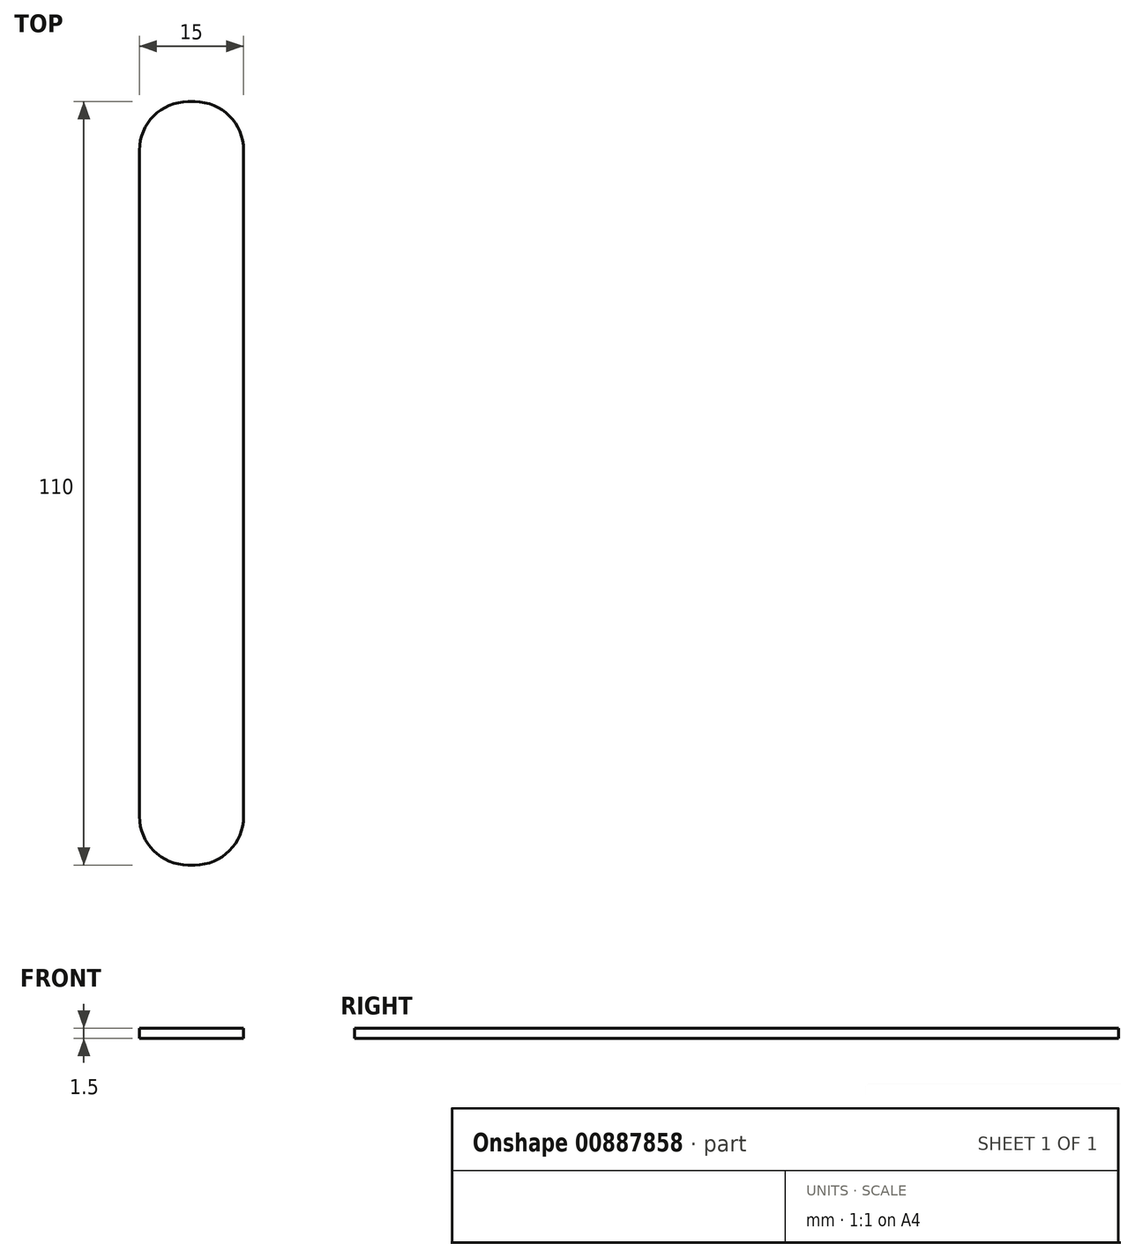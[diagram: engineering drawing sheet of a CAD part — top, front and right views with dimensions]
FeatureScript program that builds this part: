
annotation { "Feature Type Name" : "Feature", "Feature Type Description" : "" }
export const myFeature = defineFeature(function(context is Context, id is Id, definition is map)
    precondition{}
    {
        {
            var Q0;
            Q0=qCreatedBy(makeId("Top.planeOp"),FACE);
            var sketch = newSketch(context, id + "F0", { "sketchPlane" : qUnion([Q0])});
            skLineSegment(sketch, "E0.bottom", {"start": v(-25.15, 46.48) * mm, "end": v(-10.15, 46.48) * mm});
            skLineSegment(sketch, "E0.top", {"start": v(-25.15, -63.52) * mm, "end": v(-10.15, -63.52) * mm});
            skLineSegment(sketch, "E0.left", {"start": v(-25.15, 46.48) * mm, "end": v(-25.15, -63.52) * mm});
            skLineSegment(sketch, "E0.right", {"start": v(-10.15, 46.48) * mm, "end": v(-10.15, -63.52) * mm});
            skSolve(sketch);
        }
        {
            var Q0;
            Q0 = qSketchRegion(id + "F0", true);
            extrude(context, id + "F1", {"entities" : qUnion([Q0]), "depth" : 1.5 * mm, "offsetDistance" : 25 * mm});
        }
        {
            var Q0;
            Q0=makeQuery(id+"F1.opExtrude","SWEPT_EDGE",EDGE,{"disambiguationData":[OSD([sQuery(id+"F0.wireOp",EDGE,"E0.top"),sQuery(id+"F0.wireOp",EDGE,"E0.left")])]});
            var Q1;
            Q1=makeQuery(id+"F1.opExtrude","SWEPT_EDGE",EDGE,{"disambiguationData":[OSD([sQuery(id+"F0.wireOp",EDGE,"E0.bottom"),sQuery(id+"F0.wireOp",EDGE,"E0.left")])]});
            var Q2;
            Q2=makeQuery(id+"F1.opExtrude","SWEPT_EDGE",EDGE,{"disambiguationData":[OSD([sQuery(id+"F0.wireOp",EDGE,"E0.bottom"),sQuery(id+"F0.wireOp",EDGE,"E0.right")])]});
            var Q3;
            Q3=makeQuery(id+"F1.opExtrude","SWEPT_EDGE",EDGE,{"disambiguationData":[OSD([sQuery(id+"F0.wireOp",EDGE,"E0.top"),sQuery(id+"F0.wireOp",EDGE,"E0.right")])]});
            fillet(context, id + "F2", {"entities" : qUnion([Q0, Q1, Q2, Q3]), "radius" : 7 * mm, "width" : 5 * mm, "tangentPropagation" : true, "blendControlType" : BlendControlType.RADIUS, "defaultsChanged" : true, "vertexSettings" : [], "pointOnEdgeSettings" : [], "allowEdgeOverflow" : false, "smoothCorners" : false, "filletType" : FilletType.EDGE});
        }
    });
